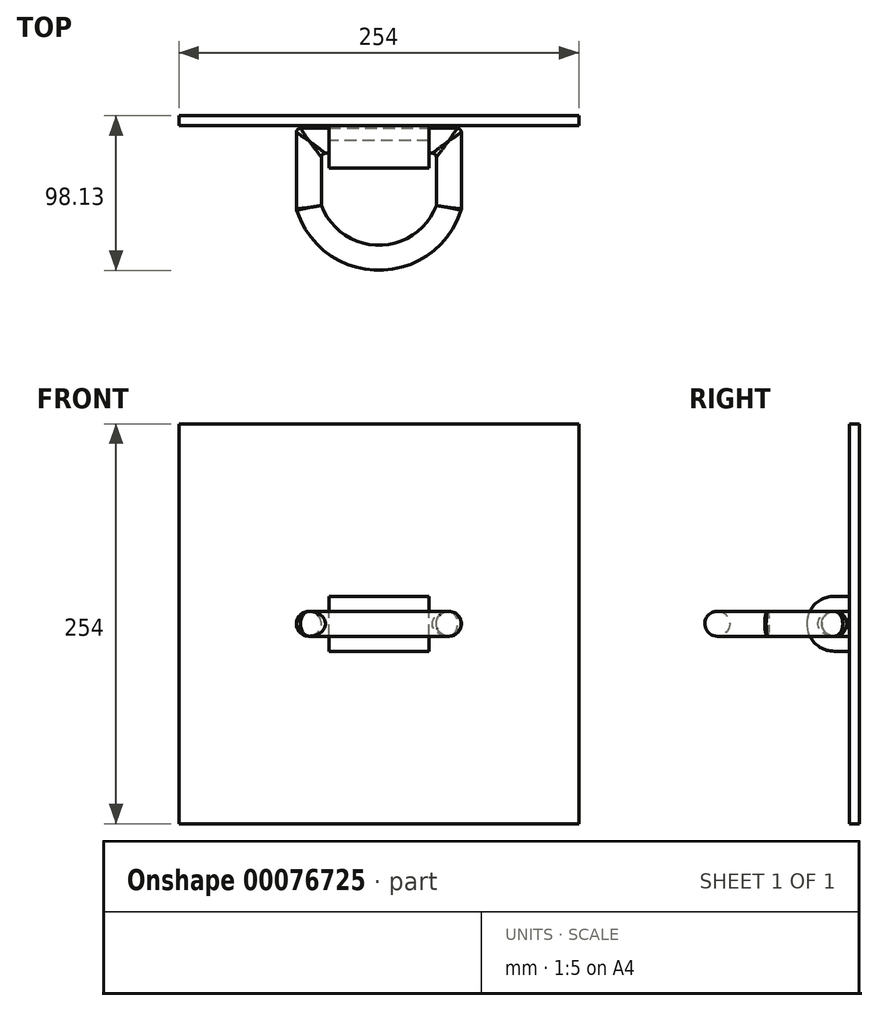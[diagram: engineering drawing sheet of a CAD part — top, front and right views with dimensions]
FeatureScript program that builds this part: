
annotation { "Feature Type Name" : "Feature", "Feature Type Description" : "" }
export const myFeature = defineFeature(function(context is Context, id is Id, definition is map)
    precondition{}
    {
        {
            var Q0;
            Q0=qCreatedBy(makeId("Front.planeOp"),FACE);
            var sketch = newSketch(context, id + "F0", { "sketchPlane" : qUnion([Q0])});
            skLineSegment(sketch, "E0.bottom", {"start": v(127, 127) * mm, "end": v(-127, 127) * mm});
            skLineSegment(sketch, "E0.top", {"start": v(127, -127) * mm, "end": v(-127, -127) * mm});
            skLineSegment(sketch, "E0.left", {"start": v(127, 127) * mm, "end": v(127, -127) * mm});
            skLineSegment(sketch, "E0.right", {"start": v(-127, 127) * mm, "end": v(-127, -127) * mm});
            skPoint(sketch, "E0.middle", {"position": v(0, 0) * mm});
            skSolve(sketch);
        }
        {
            var Q0;
            Q0 = qSketchRegion(id + "F0", true);
            extrude(context, id + "F1", {"entities" : qUnion([Q0]), "depth" : 6.35 * mm});
        }
        {
            var Q0;
            Q0=makeQuery(id+"F1.opExtrude","CAP_FACE",FACE,{"disambiguationData":[OSD([sQuery(id+"F0.wireOp",EDGE,"E0.bottom"),sQuery(id+"F0.wireOp",EDGE,"E0.top"),sQuery(id+"F0.wireOp",EDGE,"E0.left"),sQuery(id+"F0.wireOp",EDGE,"E0.right")])],"isStart":false});
            var sketch = newSketch(context, id + "F2", { "sketchPlane" : qUnion([Q0])});
            skLineSegment(sketch, "E1.bottom", {"start": v(31.75, -7.94) * mm, "end": v(-31.75, -7.94) * mm});
            skLineSegment(sketch, "E1.top", {"start": v(31.75, 7.94) * mm, "end": v(-31.75, 7.94) * mm});
            skLineSegment(sketch, "E1.left", {"start": v(31.75, -7.94) * mm, "end": v(31.75, 7.94) * mm});
            skLineSegment(sketch, "E1.right", {"start": v(-31.75, -7.94) * mm, "end": v(-31.75, 7.94) * mm});
            skPoint(sketch, "E1.middle", {"position": v(0, 0) * mm});
            skLineSegment(sketch, "E2.top", {"start": v(31.75, 17.46) * mm, "end": v(-31.75, 17.46) * mm});
            skLineSegment(sketch, "E2.left", {"start": v(31.75, 7.94) * mm, "end": v(31.75, 17.46) * mm});
            skLineSegment(sketch, "E2.right", {"start": v(-31.75, 7.94) * mm, "end": v(-31.75, 17.46) * mm});
            skLineSegment(sketch, "E3", {"start": v(0, 0) * mm, "end": v(31.75, 0) * mm});
            skSolve(sketch);
        }
        {
            var Q0;
            Q0=makeQuery(id+"F2.imprint","IMPRINT",FACE,{"disambiguationData":[TD([[makeQuery(id+"F2.imprint","IMPRINT",EDGE,{"derivedFrom":sQuery(id+"F2.wireOp",EDGE,"E1.top")}),-1.0]])]});
            extrude(context, id + "F3", {"entities" : qUnion([Q0]), "operationType" : NewBodyOperationType.ADD, "depth" : 9.52 * mm});
        }
        {
            var Q0;
            Q0=makeQuery(id+"F3.opExtrude","CAP_FACE",FACE,{"disambiguationData":[OSD([sQuery(id+"F2.wireOp",EDGE,"E1.top"),sQuery(id+"F2.wireOp",EDGE,"E2.top"),sQuery(id+"F2.wireOp",EDGE,"E2.left"),sQuery(id+"F2.wireOp",EDGE,"E2.right")])],"isStart":false});
            var sketch = newSketch(context, id + "F4", { "sketchPlane" : qUnion([Q0])});
            skLineSegment(sketch, "E4.0.0", {"start": v(-31.75, 7.94) * mm, "end": v(31.75, 7.94) * mm});
            skLineSegment(sketch, "E4.0.1", {"start": v(31.75, 7.94) * mm, "end": v(31.75, 17.46) * mm});
            skLineSegment(sketch, "E4.0.2", {"start": v(31.75, 17.46) * mm, "end": v(-31.75, 17.46) * mm});
            skLineSegment(sketch, "E4.0.3", {"start": v(-31.75, 17.46) * mm, "end": v(-31.75, 7.94) * mm});
            skLineSegment(sketch, "E5.0", {"start": v(31.75, -7.94) * mm, "end": v(-31.75, -7.94) * mm});
            skLineSegment(sketch, "E6.0", {"start": v(0, 0) * mm, "end": v(31.75, 0) * mm});
            skSolve(sketch);
        }
        {
            var Q0;
            Q0=makeQuery(id+"F4.imprint","IMPRINT",FACE,{"disambiguationData":[TD([[makeQuery(id+"F4.imprint","IMPRINT",EDGE,{"derivedFrom":sQuery(id+"F4.wireOp",EDGE,"E4.0.0")}),-1.0]])]});
            var Q1;
            Q1=sQuery(id+"F4.wireOp",EDGE,"E6.0");
            revolve(context, id + "F5", {"operationType" : NewBodyOperationType.ADD, "entities" : qUnion([Q0]), "axis" : qUnion([Q1]), "revolveType" : RevolveType.ONE_DIRECTION, "angle" : 180 * degree});
        }
        {
            var Q0;
            Q0=makeQuery(id+"F5.opRevolve","CAP_FACE",FACE,{"disambiguationData":[OSD([sQuery(id+"F4.wireOp",EDGE,"E4.0.0"),sQuery(id+"F4.wireOp",EDGE,"E4.0.1"),sQuery(id+"F4.wireOp",EDGE,"E4.0.2"),sQuery(id+"F4.wireOp",EDGE,"E4.0.3")])],"isStart":false});
            extrude(context, id + "F6", {"entities" : qUnion([Q0]), "operationType" : NewBodyOperationType.ADD, "depth" : 9.52 * mm});
        }
        {
            var Q0;
            Q0=qCreatedBy(makeId("Right.planeOp"),FACE);
            var sketch = newSketch(context, id + "F7", { "sketchPlane" : qUnion([Q0])});
            skArc(sketch, "E7.0", {"start": v(-15.88, -7.94) * mm, "mid": v(-23.81, 0) * mm, "end": v(-15.88, 7.94) * mm});
            skCircle(sketch, "E8", {"center": v(-15.88, 0) * mm, "radius": 7.94 * mm});
            skSolve(sketch);
        }
        {
            var Q0;
            Q0=qCreatedBy(makeId("Top.planeOp"),FACE);
            var sketch = newSketch(context, id + "F8", { "sketchPlane" : qUnion([Q0])});
            skPoint(sketch, "E9.0", {"position": v(0, -15.88) * mm});
            skLineSegment(sketch, "E10", {"start": v(0, -15.88) * mm, "end": v(44.4, -15.88) * mm});
            skLineSegment(sketch, "E11", {"start": v(44.4, -15.88) * mm, "end": v(44.4, -58.28) * mm});
            skLineSegment(sketch, "E12.MirrorCS", {"start": v(-44.4, -15.88) * mm, "end": v(-44.4, -58.28) * mm});
            skLineSegment(sketch, "E13.MirrorCS", {"start": v(0, -15.88) * mm, "end": v(-44.4, -15.88) * mm});
            skArc(sketch, "E14", {"start": v(-44.4, -58.28) * mm, "mid": v(0, -90.2) * mm, "end": v(44.4, -58.28) * mm});
            skSolve(sketch);
        }
        {
            var Q0;
            Q0=makeQuery(id+"F7.imprint","IMPRINT",FACE,{"disambiguationData":[TD([[makeQuery(id+"F7.imprint","IMPRINT",EDGE,{"derivedFrom":sQuery(id+"F7.wireOp",EDGE,"E8")}),1.0]])]});
            var Q1;
            Q1=sQuery(id+"F8.wireOp",EDGE,"E11");
            var Q2;
            Q2=sQuery(id+"F8.wireOp",EDGE,"E10");
            var Q3;
            Q3=sQuery(id+"F8.wireOp",EDGE,"E14");
            var Q4;
            Q4=sQuery(id+"F8.wireOp",EDGE,"E12.MirrorCS");
            var Q5;
            Q5=sQuery(id+"F8.wireOp",EDGE,"E13.MirrorCS");
            sweep(context, id + "F9", {"operationType" : NewBodyOperationType.ADD, "profiles" : qUnion([Q0]), "path" : qUnion([Q1, Q2, Q3, Q4, Q5])});
        }
        {
            var Q0;
            Q0=makeQuery(id+"F9.opSweep","MID_CAP_EDGE",EDGE,{"disambiguationData":[OSD([sQuery(id+"F7.wireOp",EDGE,"E8"),sQuery(id+"F8.wireOp",VERTEX,"E13.MirrorCS.end")])],"capPos":4.0});
            var Q1;
            Q1=makeQuery(id+"F9.opSweep","MID_CAP_EDGE",EDGE,{"disambiguationData":[OSD([sQuery(id+"F7.wireOp",EDGE,"E8"),sQuery(id+"F8.wireOp",VERTEX,"E10.end")])],"capPos":1.0});
            var Q2;
            Q2=makeQuery(id+"F9.opSweep","MID_CAP_EDGE",EDGE,{"disambiguationData":[OSD([sQuery(id+"F7.wireOp",EDGE,"E8"),sQuery(id+"F8.wireOp",VERTEX,"E14.end")]),OD(0.0)],"capPos":2.0});
            var Q3;
            Q3=makeQuery(id+"F9.opSweep","MID_CAP_EDGE",EDGE,{"disambiguationData":[OSD([sQuery(id+"F7.wireOp",EDGE,"E8"),sQuery(id+"F8.wireOp",VERTEX,"E12.MirrorCS.end")]),OD(0.0)],"capPos":3.0});
            fillet(context, id + "F10", {"entities" : qUnion([Q0, Q1, Q2, Q3]), "radius" : 2.54 * mm, "tangentPropagation" : true, "allowEdgeOverflow" : false});
        }
    });
